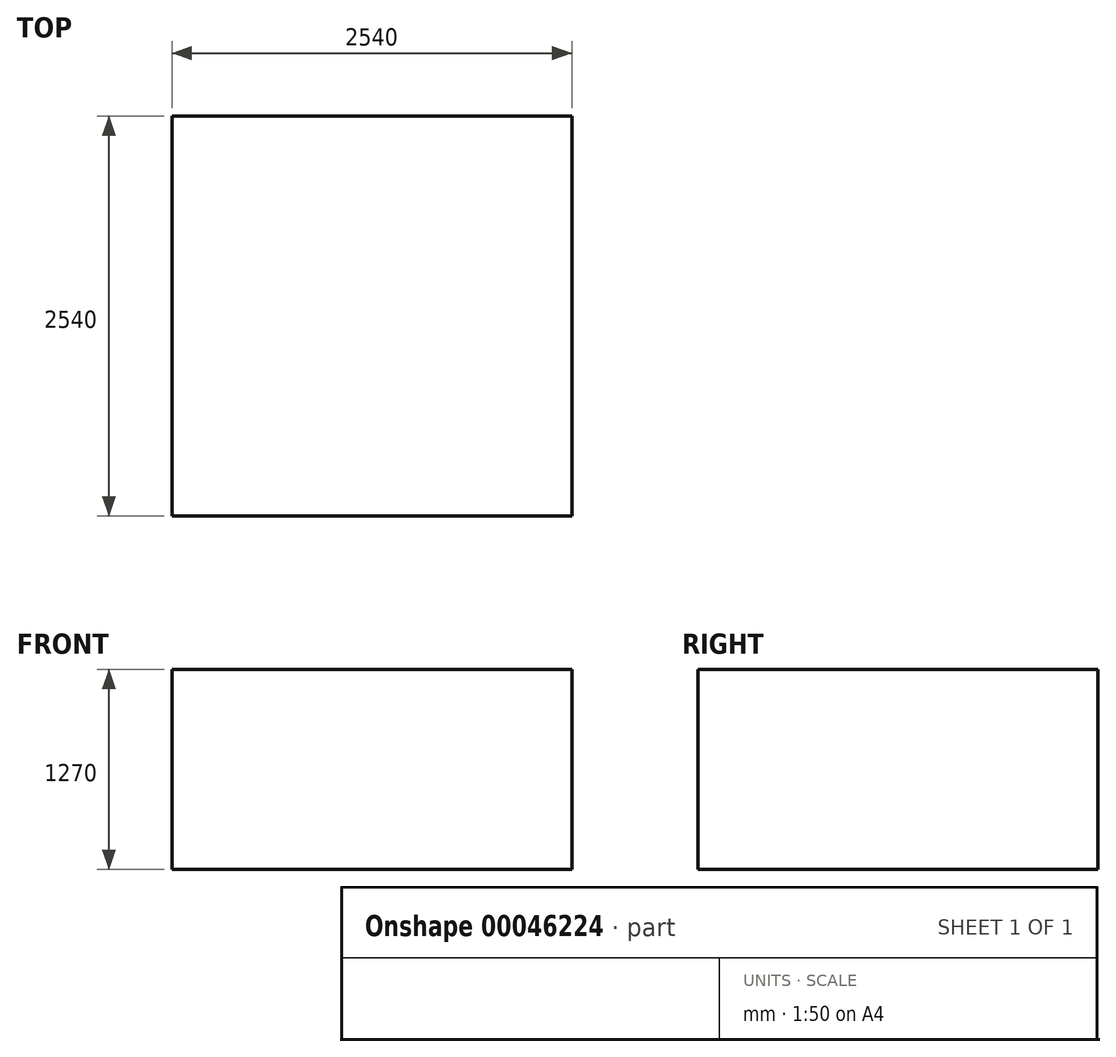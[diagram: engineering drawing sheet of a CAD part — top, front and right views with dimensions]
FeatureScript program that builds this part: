
annotation { "Feature Type Name" : "Feature", "Feature Type Description" : "" }
export const myFeature = defineFeature(function(context is Context, id is Id, definition is map)
    precondition{}
    {
        {
            var Q0;
            Q0=qCreatedBy(makeId("Top.planeOp"),FACE);
            var sketch = newSketch(context, id + "F0", { "sketchPlane" : qUnion([Q0])});
            skLineSegment(sketch, "E0.rect.bottom", {"start": v(1270, 1270) * mm, "end": v(-1270, 1270) * mm});
            skLineSegment(sketch, "E0.rect.top", {"start": v(1270, -1270) * mm, "end": v(-1270, -1270) * mm});
            skLineSegment(sketch, "E0.rect.left", {"start": v(1270, 1270) * mm, "end": v(1270, -1270) * mm});
            skLineSegment(sketch, "E0.rect.right", {"start": v(-1270, 1270) * mm, "end": v(-1270, -1270) * mm});
            skPoint(sketch, "E0.rect.middle", {"position": v(0, 0) * mm});
            skSolve(sketch);
        }
        {
            var Q0;
            Q0=makeQuery(id+"F0.imprint","IMPRINT",FACE,{"disambiguationData":[TD([[makeQuery(id+"F0.imprint","IMPRINT",EDGE,{"derivedFrom":sQuery(id+"F0.wireOp",EDGE,"E0.rect.bottom")}),1.0]])]});
            extrude(context, id + "F1", {"entities" : qUnion([Q0]), "depth" : 1270 * mm});
        }
    });
